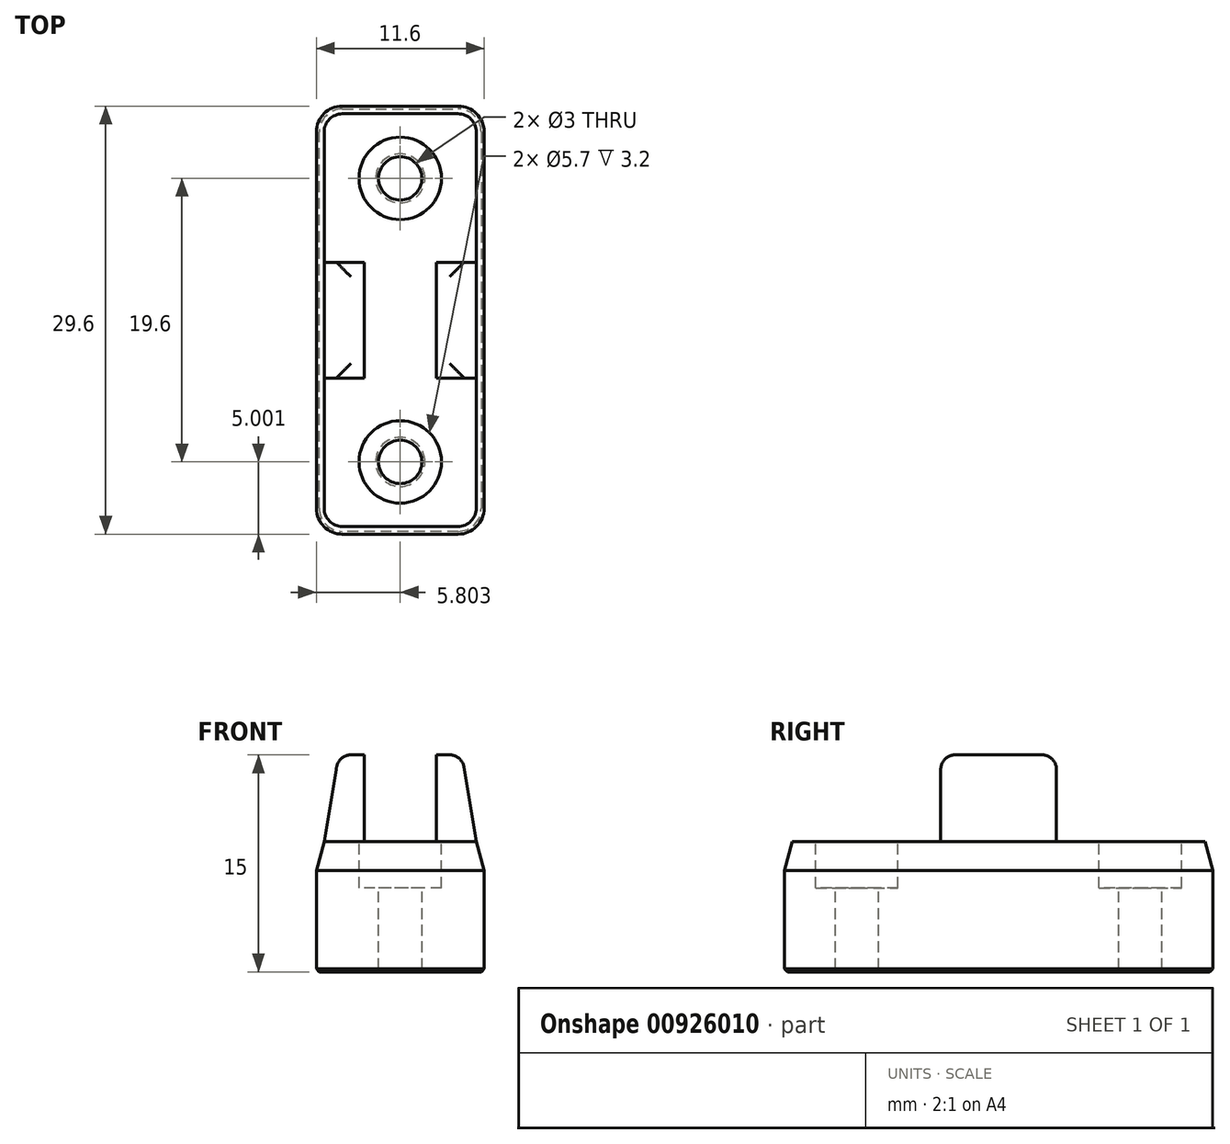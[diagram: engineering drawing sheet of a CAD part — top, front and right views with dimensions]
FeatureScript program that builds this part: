
annotation { "Feature Type Name" : "Feature", "Feature Type Description" : "" }
export const myFeature = defineFeature(function(context is Context, id is Id, definition is map)
    precondition{}
    {
        {
            var Q0;
            Q0=qCreatedBy(makeId("Top.planeOp"),FACE);
            var sketch = newSketch(context, id + "F0", { "sketchPlane" : qUnion([Q0])});
            skLineSegment(sketch, "E0.0", {"start": v(-34.48, 68.68) * mm, "end": v(-34.48, 42.68) * mm});
            skLineSegment(sketch, "E0.1", {"start": v(-44.28, 70.48) * mm, "end": v(-36.28, 70.48) * mm});
            skLineSegment(sketch, "E0.2", {"start": v(-46.08, 68.68) * mm, "end": v(-46.08, 42.68) * mm});
            skLineSegment(sketch, "E0.3", {"start": v(-44.28, 40.88) * mm, "end": v(-36.28, 40.88) * mm});
            skArc(sketch, "E1.filletArc", {"start": v(-44.28, 70.48) * mm, "mid": v(-45.55, 69.95) * mm, "end": v(-46.08, 68.68) * mm});
            skArc(sketch, "E2.filletArc", {"start": v(-34.48, 68.68) * mm, "mid": v(-35, 69.95) * mm, "end": v(-36.28, 70.48) * mm});
            skArc(sketch, "E3.filletArc", {"start": v(-36.28, 40.88) * mm, "mid": v(-35, 41.4) * mm, "end": v(-34.48, 42.68) * mm});
            skArc(sketch, "E4.filletArc", {"start": v(-46.08, 42.68) * mm, "mid": v(-45.55, 41.4) * mm, "end": v(-44.28, 40.88) * mm});
            skSolve(sketch);
        }
        {
            var Q0;
            Q0=qSketchRegion(id+"F0",true);
            extrude(context, id + "F1", {"entities" : qUnion([Q0]), "depth" : 9 * mm, "offsetDistance" : 25 * mm});
        }
        {
            var Q0;
            Q0=makeQuery(id+"F1.opExtrude","CAP_FACE",FACE,{"disambiguationData":[OSD([sQuery(id+"F0.wireOp",EDGE,"E0.0"),sQuery(id+"F0.wireOp",EDGE,"E0.1"),sQuery(id+"F0.wireOp",EDGE,"E0.2"),sQuery(id+"F0.wireOp",EDGE,"E0.3"),sQuery(id+"F0.wireOp",EDGE,"E1.filletArc"),sQuery(id+"F0.wireOp",EDGE,"E2.filletArc"),sQuery(id+"F0.wireOp",EDGE,"E3.filletArc"),sQuery(id+"F0.wireOp",EDGE,"E4.filletArc")])],"isStart":false});
            var sketch = newSketch(context, id + "F2", { "sketchPlane" : qUnion([Q0])});
            skLineSegment(sketch, "E5", {"start": v(-40.28, 70.48) * mm, "end": v(-40.28, 65.48) * mm});
            skLineSegment(sketch, "E6", {"start": v(-40.28, 40.88) * mm, "end": v(-40.28, 45.88) * mm});
            skCircle(sketch, "E7", {"center": v(-40.28, 65.48) * mm, "radius": 1.5 * mm});
            skCircle(sketch, "E8", {"center": v(-40.28, 45.88) * mm, "radius": 1.5 * mm});
            skCircle(sketch, "E9", {"center": v(-40.28, 65.48) * mm, "radius": 2.85 * mm});
            skCircle(sketch, "E10", {"center": v(-40.28, 45.88) * mm, "radius": 2.85 * mm});
            skSolve(sketch);
        }
        {
            var Q0;
            Q0=makeQuery(id+"F2.imprint","IMPRINT",FACE,{"disambiguationData":[TD([[makeQuery(id+"F2.imprint","IMPRINT",EDGE,{"derivedFrom":sQuery(id+"F2.wireOp",EDGE,"E7")}),1.0]])]});
            var Q1;
            Q1=makeQuery(id+"F2.imprint","IMPRINT",FACE,{"disambiguationData":[TD([[makeQuery(id+"F2.imprint","IMPRINT",EDGE,{"derivedFrom":sQuery(id+"F2.wireOp",EDGE,"E8")}),1.0]])]});
            extrude(context, id + "F3", {"entities" : qUnion([Q0, Q1]), "operationType" : NewBodyOperationType.REMOVE, "oppositeDirection" : true, "depth" : 25 * mm, "offsetDistance" : 25 * mm});
        }
        {
            var Q0;
            Q0=makeQuery(id+"F2.imprint","IMPRINT",FACE,{"disambiguationData":[TD([[makeQuery(id+"F2.imprint","IMPRINT",EDGE,{"derivedFrom":sQuery(id+"F2.wireOp",EDGE,"E7")}),-1.0]])]});
            var Q1;
            Q1=makeQuery(id+"F2.imprint","IMPRINT",FACE,{"disambiguationData":[TD([[makeQuery(id+"F2.imprint","IMPRINT",EDGE,{"derivedFrom":sQuery(id+"F2.wireOp",EDGE,"E8")}),-1.0]])]});
            extrude(context, id + "F4", {"entities" : qUnion([Q0, Q1]), "operationType" : NewBodyOperationType.REMOVE, "oppositeDirection" : true, "depth" : 3.2 * mm, "offsetDistance" : 25 * mm});
        }
        {
            var Q0;
            Q0=makeQuery(id+"F4.boolean.opBoolean","COPY",EDGE,{"derivedFrom":makeQuery(id+"F4.opExtrude","CAP_EDGE",EDGE,{"disambiguationData":[OSD([sQuery(id+"F2.wireOp",EDGE,"E7")])],"isStart":false})});
            var Q1;
            Q1=makeQuery(id+"F4.boolean.opBoolean","COPY",EDGE,{"derivedFrom":makeQuery(id+"F4.opExtrude","CAP_EDGE",EDGE,{"disambiguationData":[OSD([sQuery(id+"F2.wireOp",EDGE,"E8")])],"isStart":false})});
            var Q2;
            Q2=makeQuery(id+"F1.opExtrude","CAP_FACE",FACE,{"disambiguationData":[OSD([sQuery(id+"F0.wireOp",EDGE,"E0.0"),sQuery(id+"F0.wireOp",EDGE,"E0.1"),sQuery(id+"F0.wireOp",EDGE,"E0.2"),sQuery(id+"F0.wireOp",EDGE,"E0.3"),sQuery(id+"F0.wireOp",EDGE,"E1.filletArc"),sQuery(id+"F0.wireOp",EDGE,"E2.filletArc"),sQuery(id+"F0.wireOp",EDGE,"E3.filletArc"),sQuery(id+"F0.wireOp",EDGE,"E4.filletArc")])],"isStart":true});
            var Q3;
            Q3=makeQuery(id+"F4.boolean.opBoolean","COPY",EDGE,{"derivedFrom":makeQuery(id+"F4.opExtrude","CAP_EDGE",EDGE,{"disambiguationData":[OSD([sQuery(id+"F2.wireOp",EDGE,"E9")])],"isStart":true})});
            var Q4;
            Q4=makeQuery(id+"F4.boolean.opBoolean","COPY",EDGE,{"derivedFrom":makeQuery(id+"F4.opExtrude","CAP_EDGE",EDGE,{"disambiguationData":[OSD([sQuery(id+"F2.wireOp",EDGE,"E10")])],"isStart":true})});
            chamfer(context, id + "F5", {"entities" : qUnion([Q0, Q1, Q2, Q3, Q4]), "width" : 0.2 * mm, "tangentPropagation" : true});
        }
        {
            var Q0;
            Q0=makeQuery(id+"F1.opExtrude","CAP_EDGE",EDGE,{"disambiguationData":[OSD([sQuery(id+"F0.wireOp",EDGE,"E0.0")])],"isStart":false});
            chamfer(context, id + "F6", {"entities" : qUnion([Q0]), "chamferType" : ChamferType.OFFSET_ANGLE, "width" : 2 * mm, "oppositeDirection" : false, "angle" : 15 * degree, "tangentPropagation" : true});
        }
        {
            var Q0;
            Q0=makeQuery(id+"F1.opExtrude","CAP_FACE",FACE,{"disambiguationData":[OSD([sQuery(id+"F0.wireOp",EDGE,"E0.0"),sQuery(id+"F0.wireOp",EDGE,"E0.1"),sQuery(id+"F0.wireOp",EDGE,"E0.2"),sQuery(id+"F0.wireOp",EDGE,"E0.3"),sQuery(id+"F0.wireOp",EDGE,"E1.filletArc"),sQuery(id+"F0.wireOp",EDGE,"E2.filletArc"),sQuery(id+"F0.wireOp",EDGE,"E3.filletArc"),sQuery(id+"F0.wireOp",EDGE,"E4.filletArc")])],"isStart":false});
            var sketch = newSketch(context, id + "F7", { "sketchPlane" : qUnion([Q0])});
            skLineSegment(sketch, "E11", {"start": v(-37.78, 52.68) * mm, "end": v(-35.01, 52.68) * mm});
            skLineSegment(sketch, "E12", {"start": v(-35.01, 52.68) * mm, "end": v(-35.01, 58.68) * mm});
            skLineSegment(sketch, "E13", {"start": v(-45.54, 58.68) * mm, "end": v(-45.54, 52.68) * mm});
            skLineSegment(sketch, "E14", {"start": v(-45.54, 52.68) * mm, "end": v(-42.78, 52.68) * mm});
            skLineSegment(sketch, "E15.left", {"start": v(-37.78, 58.68) * mm, "end": v(-37.78, 52.68) * mm});
            skLineSegment(sketch, "E15.right", {"start": v(-42.78, 58.68) * mm, "end": v(-42.78, 52.68) * mm});
            skPoint(sketch, "E15.middle", {"position": v(-40.28, 55.68) * mm});
            skPoint(sketch, "E16.orphan", {"position": v(-45.54, 55.68) * mm});
            skPoint(sketch, "E17.end.orphan", {"position": v(-35.01, 55.68) * mm});
            skPoint(sketch, "E18.orphan", {"position": v(-40.28, 52.68) * mm});
            skLineSegment(sketch, "E19.trimOffspring", {"start": v(-42.78, 58.68) * mm, "end": v(-45.54, 58.68) * mm});
            skLineSegment(sketch, "E20", {"start": v(-37.78, 58.68) * mm, "end": v(-35.01, 58.68) * mm});
            skSolve(sketch);
        }
        {
            var Q0;
            Q0 = qSketchRegion(id + "F7", true);
            extrude(context, id + "F8", {"entities" : qUnion([Q0]), "operationType" : NewBodyOperationType.ADD, "depth" : 6 * mm, "offsetDistance" : 25 * mm});
        }
        {
            var Q0;
            Q0=makeQuery(id+"F8.opExtrude","CAP_EDGE",EDGE,{"disambiguationData":[OSD([sQuery(id+"F7.wireOp",EDGE,"E12")])],"isStart":false});
            var Q1;
            Q1=makeQuery(id+"F8.opExtrude","CAP_EDGE",EDGE,{"disambiguationData":[OSD([sQuery(id+"F7.wireOp",EDGE,"E13")])],"isStart":false});
            chamfer(context, id + "F9", {"entities" : qUnion([Q0, Q1]), "chamferType" : ChamferType.TWO_OFFSETS, "width1" : 1 * mm, "oppositeDirection" : false, "width2" : 6 * mm, "tangentPropagation" : true});
        }
        {
            var Q0;
            Q0=makeQuery(id+"F8.opExtrude","SWEPT_FACE",FACE,{"disambiguationData":[OSD([sQuery(id+"F7.wireOp",EDGE,"E20")])]});
            var Q1;
            Q1=makeQuery(id+"F8.opExtrude","SWEPT_FACE",FACE,{"disambiguationData":[OSD([sQuery(id+"F7.wireOp",EDGE,"E19.trimOffspring")])]});
            extrude(context, id + "F10", {"entities" : qUnion([Q0, Q1]), "operationType" : NewBodyOperationType.ADD, "depth" : 1 * mm, "offsetDistance" : 25 * mm});
        }
        {
            var Q0;
            Q0=makeQuery(id+"F8.opExtrude","SWEPT_FACE",FACE,{"disambiguationData":[OSD([sQuery(id+"F7.wireOp",EDGE,"E14")])]});
            var Q1;
            Q1=makeQuery(id+"F8.opExtrude","SWEPT_FACE",FACE,{"disambiguationData":[OSD([sQuery(id+"F7.wireOp",EDGE,"E11")])]});
            extrude(context, id + "F11", {"entities" : qUnion([Q0, Q1]), "operationType" : NewBodyOperationType.ADD, "depth" : 1 * mm, "offsetDistance" : 25 * mm});
        }
        {
            var Q0;
            {var subQ0=sQuery(id+"F7.wireOp",EDGE,"E20");var subQ1=sQuery(id+"F7.wireOp",EDGE,"E15.left");var subQ2=sQuery(id+"F7.wireOp",EDGE,"E12");var subQ3=sQuery(id+"F7.wireOp",EDGE,"E11");Q0=makeQuery(id+"F11.boolean.opBoolean","MERGE",EDGE,{"derivedFrom":[makeQuery(id+"F10.boolean.opBoolean","MERGE",EDGE,{"derivedFrom":[makeQuery(id+"F9.opChamfer","BLEND_EDGE",EDGE,{"blendedFrom":[makeQuery(id+"F8.opExtrude","CAP_EDGE",EDGE,{"disambiguationData":[OSD([subQ2])],"isStart":false}),makeQuery(id+"F8.opExtrude","CAP_FACE",FACE,{"disambiguationData":[OSD([subQ3,subQ2,subQ1,subQ0])],"isStart":false})],"blendedInto":[makeQuery(id+"F8.opExtrude","CAP_FACE",FACE,{"disambiguationData":[OSD([subQ3,subQ2,subQ1,subQ0])],"isStart":false})]}),makeQuery(id+"F10.opExtrude","SWEPT_EDGE",EDGE,{"disambiguationData":[OSD([subQ3,subQ2,subQ1,subQ0])]})]}),makeQuery(id+"F11.opExtrude","SWEPT_EDGE",EDGE,{"disambiguationData":[OSD([subQ3,subQ2,subQ1,subQ0])]})]});}
            var Q1;
            {var subQ0=sQuery(id+"F7.wireOp",EDGE,"E19.trimOffspring");var subQ1=sQuery(id+"F7.wireOp",EDGE,"E15.right");var subQ2=sQuery(id+"F7.wireOp",EDGE,"E14");var subQ3=sQuery(id+"F7.wireOp",EDGE,"E13");Q1=makeQuery(id+"F11.boolean.opBoolean","MERGE",EDGE,{"derivedFrom":[makeQuery(id+"F10.boolean.opBoolean","MERGE",EDGE,{"derivedFrom":[makeQuery(id+"F9.opChamfer","BLEND_EDGE",EDGE,{"blendedFrom":[makeQuery(id+"F8.opExtrude","CAP_EDGE",EDGE,{"disambiguationData":[OSD([subQ3])],"isStart":false}),makeQuery(id+"F8.opExtrude","CAP_FACE",FACE,{"disambiguationData":[OSD([subQ3,subQ2,subQ1,subQ0])],"isStart":false})],"blendedInto":[makeQuery(id+"F8.opExtrude","CAP_FACE",FACE,{"disambiguationData":[OSD([subQ3,subQ2,subQ1,subQ0])],"isStart":false})]}),makeQuery(id+"F10.opExtrude","SWEPT_EDGE",EDGE,{"disambiguationData":[OSD([subQ3,subQ2,subQ1,subQ0])]})]}),makeQuery(id+"F11.opExtrude","SWEPT_EDGE",EDGE,{"disambiguationData":[OSD([subQ3,subQ2,subQ1,subQ0])]})]});}
            var Q2;
            {var subQ0=sQuery(id+"F7.wireOp",EDGE,"E11");Q2=makeQuery(id+"F11.opExtrude","CAP_EDGE",EDGE,{"disambiguationData":[OSD([subQ0]),TDD([makeQuery(id+"F8.opExtrude","CAP_EDGE",EDGE,{"disambiguationData":[OSD([subQ0])],"isStart":true})])],"isStart":false});}
            var Q3;
            {var subQ0=sQuery(id+"F7.wireOp",EDGE,"E14");Q3=makeQuery(id+"F11.opExtrude","CAP_EDGE",EDGE,{"disambiguationData":[OSD([subQ0]),TDD([makeQuery(id+"F8.opExtrude","CAP_EDGE",EDGE,{"disambiguationData":[OSD([subQ0])],"isStart":true})])],"isStart":false});}
            var Q4;
            {var subQ0=sQuery(id+"F7.wireOp",EDGE,"E20");Q4=makeQuery(id+"F10.opExtrude","CAP_EDGE",EDGE,{"disambiguationData":[OSD([subQ0]),TDD([makeQuery(id+"F8.opExtrude","CAP_EDGE",EDGE,{"disambiguationData":[OSD([subQ0])],"isStart":true})])],"isStart":false});}
            var Q5;
            {var subQ0=sQuery(id+"F7.wireOp",EDGE,"E19.trimOffspring");Q5=makeQuery(id+"F10.opExtrude","CAP_EDGE",EDGE,{"disambiguationData":[OSD([subQ0]),TDD([makeQuery(id+"F8.opExtrude","CAP_EDGE",EDGE,{"disambiguationData":[OSD([subQ0])],"isStart":true})])],"isStart":false});}
            fillet(context, id + "F12", {"entities" : qUnion([Q0, Q1, Q2, Q3, Q4, Q5]), "radius" : 1 * mm, "tangentPropagation" : true, "allowEdgeOverflow" : false});
        }
    });
